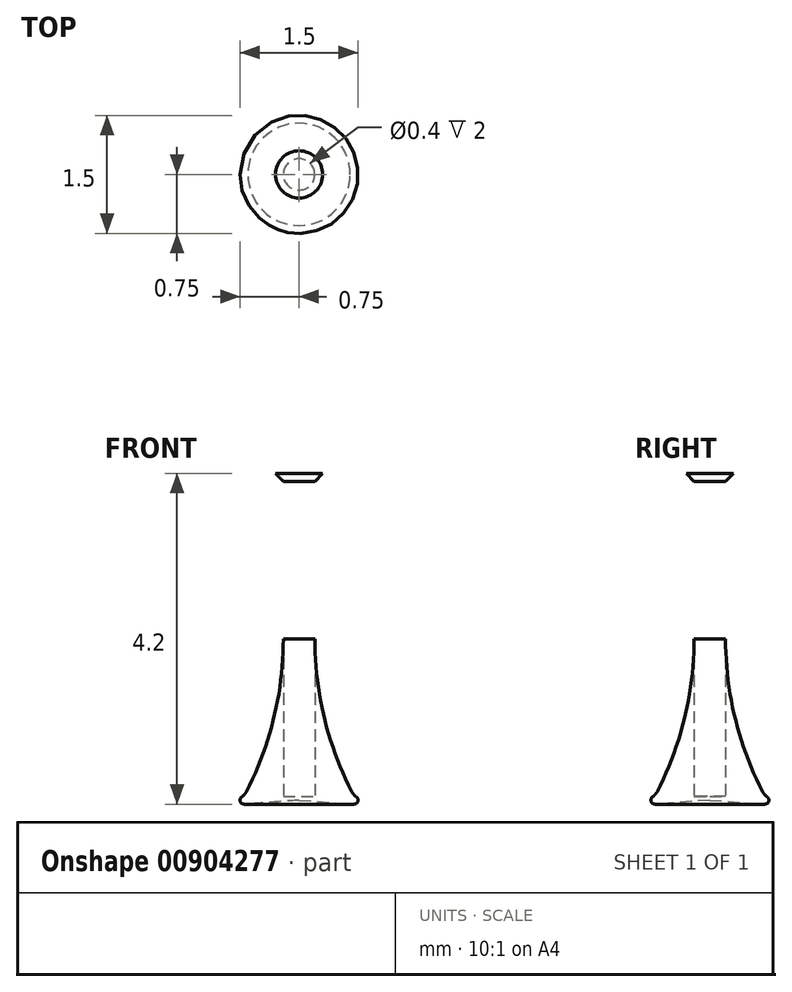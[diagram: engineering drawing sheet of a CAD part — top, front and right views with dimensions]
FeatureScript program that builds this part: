
annotation { "Feature Type Name" : "Feature", "Feature Type Description" : "" }
export const myFeature = defineFeature(function(context is Context, id is Id, definition is map)
    precondition{}
    {
        {
            var Q0;
            Q0=qCreatedBy(makeId("Front.planeOp"),FACE);
            var sketch = newSketch(context, id + "F0", { "sketchPlane" : qUnion([Q0])});
            skLineSegment(sketch, "E0.bottom", {"start": v(0, 0) * mm, "end": v(-0.7, 0) * mm});
            skLineSegment(sketch, "E0.top", {"start": v(0, 0.1) * mm, "end": v(-0.7, 0.1) * mm});
            skLineSegment(sketch, "E0.left", {"start": v(0, 0) * mm, "end": v(0, 0.1) * mm});
            skLineSegment(sketch, "E0.right", {"start": v(-0.7, 0) * mm, "end": v(-0.7, 0.1) * mm});
            skArc(sketch, "E1", {"start": v(-0.7, 0.1) * mm, "mid": v(-0.75, 0.05) * mm, "end": v(-0.7, 0) * mm});
            skLineSegment(sketch, "E2.bottom", {"start": v(0, 0.1) * mm, "end": v(-0.2, 0.1) * mm});
            skLineSegment(sketch, "E2.top", {"start": v(0, 4.1) * mm, "end": v(-0.2, 4.1) * mm});
            skLineSegment(sketch, "E2.left", {"start": v(0, 0.1) * mm, "end": v(0, 4.1) * mm});
            skLineSegment(sketch, "E2.right", {"start": v(-0.2, 0.1) * mm, "end": v(-0.2, 4.1) * mm});
            skArc(sketch, "E3", {"start": v(-0.7, 0.1) * mm, "mid": v(-0.33, 1.07) * mm, "end": v(-0.2, 2.1) * mm});
            skLineSegment(sketch, "E4", {"start": v(-0.7, 0) * mm, "end": v(-0.65, 0) * mm});
            skLineSegment(sketch, "E5", {"start": v(-0.65, 0) * mm, "end": v(0, 0.05) * mm});
            skLineSegment(sketch, "E6.bottom", {"start": v(0, 4.1) * mm, "end": v(-0.6, 4.1) * mm});
            skLineSegment(sketch, "E6.top", {"start": v(0, 4.2) * mm, "end": v(-0.6, 4.2) * mm});
            skLineSegment(sketch, "E6.left", {"start": v(0, 4.1) * mm, "end": v(0, 4.2) * mm});
            skLineSegment(sketch, "E6.right", {"start": v(-0.6, 4.1) * mm, "end": v(-0.6, 4.2) * mm});
            skSolve(sketch);
        }
        {
            var Q0;
            Q0=makeQuery(id+"F0.imprint","IMPRINT",FACE,{"disambiguationData":[TD([[makeQuery(id+"F0.imprint","IMPRINT",EDGE,{"derivedFrom":sQuery(id+"F0.wireOp",EDGE,"E0.top")}),1.0]])]});
            var Q1;
            Q1=makeQuery(id+"F0.imprint","IMPRINT",FACE,{"disambiguationData":[TD([[makeQuery(id+"F0.imprint","IMPRINT",EDGE,{"derivedFrom":sQuery(id+"F0.wireOp",EDGE,"E0.right")}),1.0]])]});
            var Q2;
            {var subQ0=sQuery(id+"F0.wireOp",EDGE,"E0.top");Q2=makeQuery(id+"F0.imprint","IMPRINT",FACE,{"disambiguationData":[TD([[makeQuery(id+"F0.imprint","IMPRINT",EDGE,{"derivedFrom":subQ0}),-1.0]])]});}
            var Q3;
            {var subQ4=sQuery(id+"F0.wireOp",EDGE,"E2.bottom");Q3=makeQuery(id+"F0.imprint","IMPRINT",FACE,{"disambiguationData":[TD([[makeQuery(id+"F0.imprint","IMPRINT",EDGE,{"derivedFrom":subQ4}),-1.0]])]});}
            var Q4;
            Q4=makeQuery(id+"F0.imprint","IMPRINT",FACE,{"disambiguationData":[TD([[makeQuery(id+"F0.imprint","IMPRINT",EDGE,{"derivedFrom":sQuery(id+"F0.wireOp",EDGE,"E6.top")}),1.0]])]});
            var Q5;
            Q5=sQuery(id+"F0.wireOp",EDGE,"E2.left");
            revolve(context, id + "F1", {"surfaceOperationType" : NewSurfaceOperationType.NEW, "entities" : qUnion([Q0, Q1, Q2, Q3, Q4]), "axis" : qUnion([Q5]), "revolveType" : RevolveType.FULL});
        }
        {
            var Q0;
            Q0=makeQuery(id+"F1.opRevolve","SWEPT_EDGE",EDGE,{"disambiguationData":[OSD([sQuery(id+"F0.wireOp",EDGE,"E0.top"),sQuery(id+"F0.wireOp",EDGE,"E0.right"),sQuery(id+"F0.wireOp",EDGE,"E1"),sQuery(id+"F0.wireOp",EDGE,"E3")])]});
            fillet(context, id + "F2", {"entities" : qUnion([Q0]), "radius" : 0.2 * mm, "tangentPropagation" : true, "allowEdgeOverflow" : false});
        }
        {
            var Q0;
            Q0=makeQuery(id+"F1.opRevolve","SWEPT_EDGE",EDGE,{"disambiguationData":[OSD([sQuery(id+"F0.wireOp",EDGE,"E2.right"),sQuery(id+"F0.wireOp",EDGE,"E6.bottom")])]});
            chamfer(context, id + "F3", {"entities" : qUnion([Q0]), "width" : 0.4 * mm, "tangentPropagation" : true});
        }
    });
